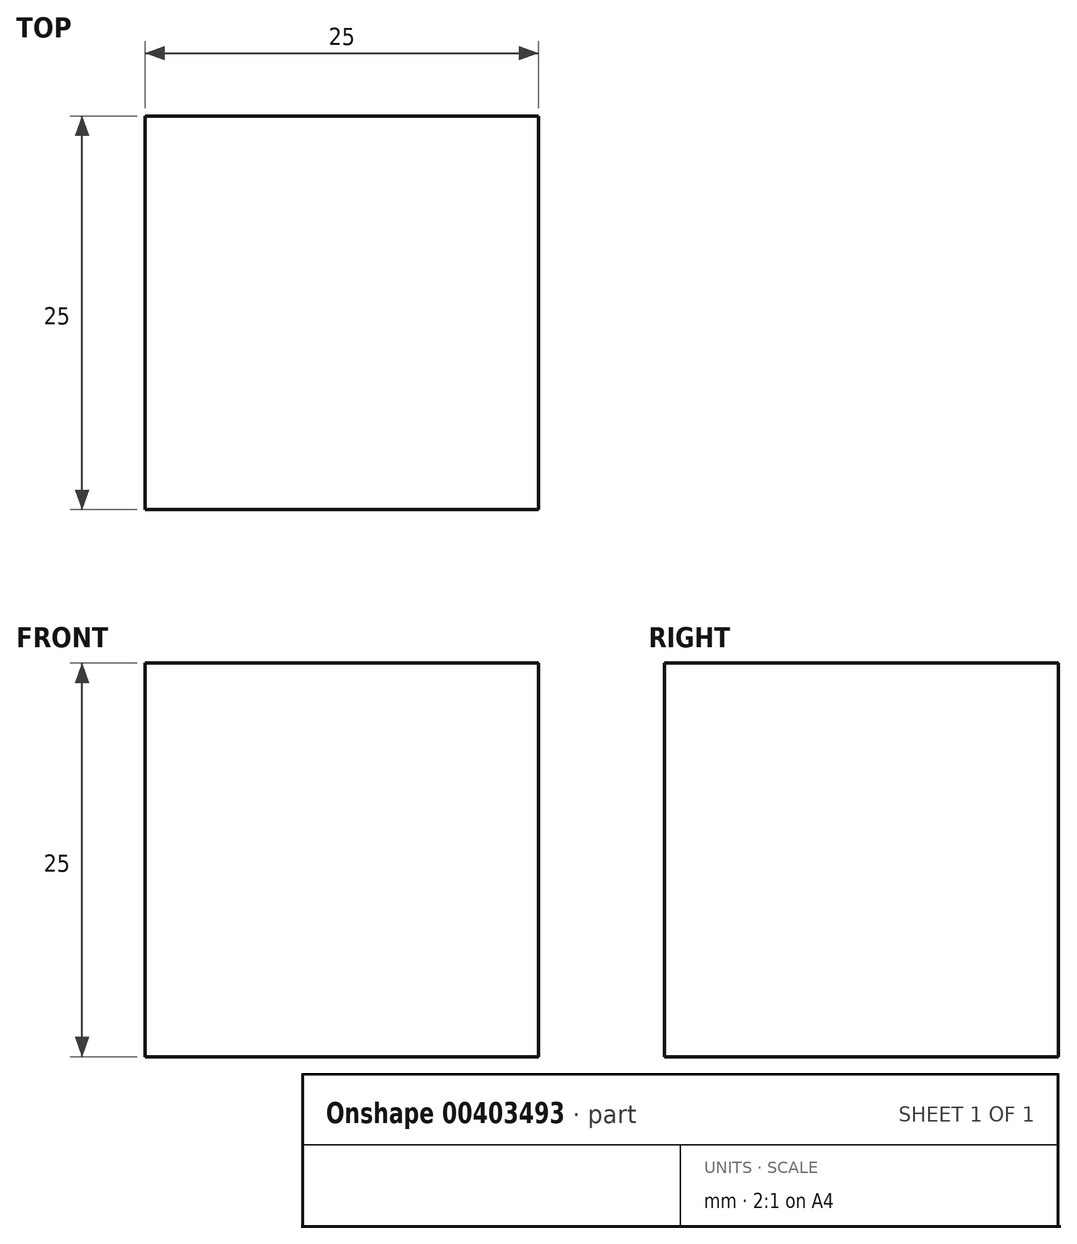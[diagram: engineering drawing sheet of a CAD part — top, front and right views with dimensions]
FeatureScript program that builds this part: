
annotation { "Feature Type Name" : "Feature", "Feature Type Description" : "" }
export const myFeature = defineFeature(function(context is Context, id is Id, definition is map)
    precondition{}
    {
        {
            var Q0;
            Q0=qCreatedBy(makeId("Front.planeOp"),FACE);
            var sketch = newSketch(context, id + "F0", { "sketchPlane" : qUnion([Q0])});
            skLineSegment(sketch, "E0.bottom", {"start": v(0, 0) * mm, "end": v(25, 0) * mm});
            skLineSegment(sketch, "E0.top", {"start": v(0, 25) * mm, "end": v(25, 25) * mm});
            skLineSegment(sketch, "E0.left", {"start": v(0, 0) * mm, "end": v(0, 25) * mm});
            skLineSegment(sketch, "E0.right", {"start": v(25, 0) * mm, "end": v(25, 25) * mm});
            skSolve(sketch);
        }
        {
            var Q0;
            Q0=makeQuery(id+"F0.imprint","IMPRINT",FACE,{"disambiguationData":[TD([[makeQuery(id+"F0.imprint","IMPRINT",EDGE,{"derivedFrom":sQuery(id+"F0.wireOp",EDGE,"E0.bottom")}),1.0]])]});
            var Q1;
            Q1=qSketchRegion(id+"F0",true);
            extrude(context, id + "F1", {"entities" : qUnion([Q0, Q1]), "depth" : 25 * mm});
        }
    });
